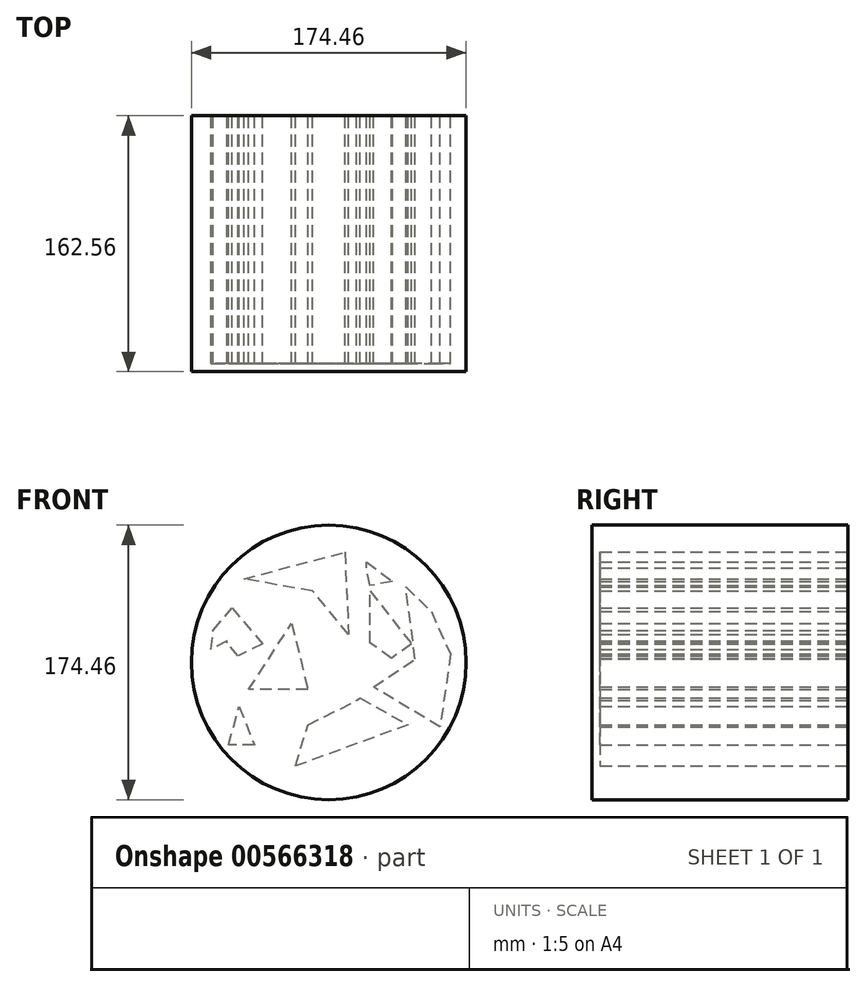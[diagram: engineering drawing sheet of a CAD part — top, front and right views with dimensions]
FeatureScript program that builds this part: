
annotation { "Feature Type Name" : "Feature", "Feature Type Description" : "" }
export const myFeature = defineFeature(function(context is Context, id is Id, definition is map)
    precondition{}
    {
        {
            var Q0;
            Q0=qCreatedBy(makeId("Front.planeOp"),FACE);
            var sketch = newSketch(context, id + "F0", { "sketchPlane" : qUnion([Q0])});
            skCircle(sketch, "E0", {"center": v(0, 2.96) * mm, "radius": 76.39 * mm});
            skLineSegment(sketch, "E1", {"start": v(-74.5, 19.82) * mm, "end": v(-55.23, 19.82) * mm});
            skLineSegment(sketch, "E2", {"start": v(-55.23, 19.82) * mm, "end": v(-44.99, 9.16) * mm});
            skLineSegment(sketch, "E3", {"start": v(-44.99, 9.16) * mm, "end": v(-44.99, -5.66) * mm});
            skLineSegment(sketch, "E4", {"start": v(-44.99, -5.66) * mm, "end": v(-22.1, -5.66) * mm});
            skLineSegment(sketch, "E5", {"start": v(-22.1, -3.5) * mm, "end": v(-22.1, 12.4) * mm});
            skLineSegment(sketch, "E6", {"start": v(-21.28, 11.85) * mm, "end": v(-3.77, 16.7) * mm});
            skLineSegment(sketch, "E7", {"start": v(-3.77, 16.7) * mm, "end": v(2.7, 35.83) * mm});
            skLineSegment(sketch, "E8", {"start": v(2.7, 35.83) * mm, "end": v(25.6, 35.83) * mm});
            skLineSegment(sketch, "E9", {"start": v(25.6, 35.83) * mm, "end": v(-12.12, 57.65) * mm});
            skLineSegment(sketch, "E10", {"start": v(-12.12, 57.65) * mm, "end": v(20.33, 76.6) * mm});
            skLineSegment(sketch, "E11", {"start": v(-3.77, 16.7) * mm, "end": v(32.87, 9.16) * mm});
            skLineSegment(sketch, "E12", {"start": v(32.87, 9.16) * mm, "end": v(28.86, -10.3) * mm});
            skLineSegment(sketch, "E13", {"start": v(29.9, -10.5) * mm, "end": v(54.69, -10.5) * mm});
            skLineSegment(sketch, "E14", {"start": v(54.69, -10.5) * mm, "end": v(11.58, -43.37) * mm});
            skLineSegment(sketch, "E15", {"start": v(11.58, -43.37) * mm, "end": v(42.3, -49.84) * mm});
            skLineSegment(sketch, "E16", {"start": v(42.3, -49.84) * mm, "end": v(54.69, -35.56) * mm});
            skLineSegment(sketch, "E17", {"start": v(55.76, -35.56) * mm, "end": v(63.58, -38.8) * mm});
            skLineSegment(sketch, "E18", {"start": v(-22.1, -3.5) * mm, "end": v(-22.1, -5.66) * mm});
            skLineSegment(sketch, "E19", {"start": v(-44.99, -5.66) * mm, "end": v(-27.75, -45.8) * mm});
            skLineSegment(sketch, "E20", {"start": v(-27.75, -45.8) * mm, "end": v(-3.77, -24.51) * mm});
            skLineSegment(sketch, "E21", {"start": v(-3.77, -24.51) * mm, "end": v(25.6, -32.7) * mm});
            skLineSegment(sketch, "E22", {"start": v(-21.28, 11.85) * mm, "end": v(-36.9, 38.25) * mm});
            skLineSegment(sketch, "E23", {"start": v(-36.9, 38.25) * mm, "end": v(2.7, 35.83) * mm});
            skLineSegment(sketch, "E24", {"start": v(-36.9, 38.25) * mm, "end": v(-51.77, 42.4) * mm});
            skLineSegment(sketch, "E25", {"start": v(-51.45, 42.56) * mm, "end": v(-31.05, 72.75) * mm});
            skLineSegment(sketch, "E26", {"start": v(25.6, 35.83) * mm, "end": v(48.22, 16.7) * mm});
            skLineSegment(sketch, "E27", {"start": v(48.22, 16.7) * mm, "end": v(62.82, 46.42) * mm});
            skLineSegment(sketch, "E28", {"start": v(-36.89, -24.51) * mm, "end": v(-61.06, -42.94) * mm});
            skLineSegment(sketch, "E29", {"start": v(-22.1, -40.78) * mm, "end": v(20.33, -52.59) * mm});
            skLineSegment(sketch, "E30", {"start": v(20.33, -54.96) * mm, "end": v(-8.08, -73) * mm});
            skLineSegment(sketch, "E31", {"start": v(20.33, -52.59) * mm, "end": v(20.33, -54.96) * mm});
            skLineSegment(sketch, "E32", {"start": v(32.87, 9.16) * mm, "end": v(54.69, 9.16) * mm});
            skLineSegment(sketch, "E33", {"start": v(53.88, 8.62) * mm, "end": v(48.22, 16.7) * mm});
            skSolve(sketch);
        }
        {
            var Q0;
            Q0=qCreatedBy(makeId("Front.planeOp"),FACE);
            var sketch = newSketch(context, id + "F1", { "sketchPlane" : qUnion([Q0])});
            skCircle(sketch, "E34", {"center": v(0, 0) * mm, "radius": 87.23 * mm});
            skLineSegment(sketch, "E35", {"start": v(60.07, 50.38) * mm, "end": v(46.6, 24.79) * mm});
            skLineSegment(sketch, "E36", {"start": v(46.6, 24.79) * mm, "end": v(0, 56.04) * mm});
            skLineSegment(sketch, "E37", {"start": v(0, 56.04) * mm, "end": v(24.25, 75.97) * mm});
            skLineSegment(sketch, "E38", {"start": v(65.46, -35.83) * mm, "end": v(51.45, -30.71) * mm});
            skLineSegment(sketch, "E39", {"start": v(51.45, -30.71) * mm, "end": v(42.03, -42.03) * mm});
            skLineSegment(sketch, "E40", {"start": v(42.03, -42.03) * mm, "end": v(24.25, -42.03) * mm});
            skLineSegment(sketch, "E41", {"start": v(25.86, -41.22) * mm, "end": v(61.15, -7.81) * mm});
            skLineSegment(sketch, "E42", {"start": v(61.15, -7.81) * mm, "end": v(35.83, -7.81) * mm});
            skLineSegment(sketch, "E43", {"start": v(35.83, -7.27) * mm, "end": v(35.83, 5.12) * mm});
            skLineSegment(sketch, "E44", {"start": v(36.1, 5.12) * mm, "end": v(60.07, 5.12) * mm});
            skLineSegment(sketch, "E45", {"start": v(60.07, 6.2) * mm, "end": v(56.03, 15.09) * mm});
            skLineSegment(sketch, "E46", {"start": v(56.03, 15.09) * mm, "end": v(65.73, 41.76) * mm});
            skLineSegment(sketch, "E47", {"start": v(-14.82, -71.93) * mm, "end": v(11.58, -54.42) * mm});
            skLineSegment(sketch, "E48", {"start": v(11.58, -54.42) * mm, "end": v(-22.36, -45.53) * mm});
            skLineSegment(sketch, "E49", {"start": v(-22.36, -45.53) * mm, "end": v(-29.36, -50.38) * mm});
            skLineSegment(sketch, "E50", {"start": v(-29.36, -50.38) * mm, "end": v(-37.45, -32.06) * mm});
            skLineSegment(sketch, "E51", {"start": v(-37.45, -32.06) * mm, "end": v(-56.84, -46.88) * mm});
            skLineSegment(sketch, "E52", {"start": v(-64.92, -36.64) * mm, "end": v(-44.72, -22.63) * mm});
            skLineSegment(sketch, "E53", {"start": v(-44.72, -22.63) * mm, "end": v(-51.18, 8.62) * mm});
            skLineSegment(sketch, "E54", {"start": v(-51.18, 8.62) * mm, "end": v(-56.84, 14.55) * mm});
            skLineSegment(sketch, "E55", {"start": v(-58.46, 14.55) * mm, "end": v(-74.9, 14.55) * mm});
            skLineSegment(sketch, "E56", {"start": v(-41.76, 66.81) * mm, "end": v(-56.84, 40.95) * mm});
            skLineSegment(sketch, "E57", {"start": v(-55.76, 40.95) * mm, "end": v(-40.4, 36.1) * mm});
            skLineSegment(sketch, "E58", {"start": v(-40.4, 36.1) * mm, "end": v(-25.05, 12.12) * mm});
            skLineSegment(sketch, "E59", {"start": v(-25.05, 12.12) * mm, "end": v(-25.05, 0) * mm});
            skLineSegment(sketch, "E60", {"start": v(-24.78, -1.35) * mm, "end": v(-40.4, -1.35) * mm});
            skLineSegment(sketch, "E61", {"start": v(-39.6, -1.35) * mm, "end": v(-44.72, -5.12) * mm});
            skLineSegment(sketch, "E62", {"start": v(0, 33.68) * mm, "end": v(-6.47, 21.28) * mm});
            skLineSegment(sketch, "E63", {"start": v(-6.47, 21.28) * mm, "end": v(-20.07, 12.57) * mm});
            skLineSegment(sketch, "E64", {"start": v(0, 33.68) * mm, "end": v(-33.67, 33.68) * mm});
            skLineSegment(sketch, "E65", {"start": v(22.1, -35.3) * mm, "end": v(-2.42, -28.02) * mm});
            skLineSegment(sketch, "E66", {"start": v(-2.42, -28.02) * mm, "end": v(-17.24, -41.22) * mm});
            skSolve(sketch);
        }
        {
            var Q0;
            Q0=makeQuery(id+"F0.imprint","IMPRINT",FACE,{"disambiguationData":[TD([[makeQuery(id+"F0.imprint","IMPRINT",EDGE,{"derivedFrom":sQuery(id+"F0.wireOp",EDGE,"E6")}),1.0]])]});
            var Q1;
            Q1=makeQuery(id+"F1.imprint","IMPRINT",FACE,{"disambiguationData":[TD([[makeQuery(id+"F1.imprint","IMPRINT",EDGE,{"derivedFrom":sQuery(id+"F1.wireOp",EDGE,"E34")}),1.0]])]});
            extrude(context, id + "F2", {"entities" : qUnion([Q0, Q1]), "depth" : 162.56 * mm, "offsetDistance" : 25.4 * mm});
        }
        {
            var Q0;
            Q0=makeQuery(id+"F2.opExtrude","SWEPT_BODY",BODY,{"disambiguationData":[OSD([sQuery(id+"F0.wireOp",EDGE,"E6"),sQuery(id+"F0.wireOp",EDGE,"E7"),sQuery(id+"F0.wireOp",EDGE,"E22"),sQuery(id+"F0.wireOp",EDGE,"E23")])]});
            deleteBodies(context, id + "F3", {"entities" : qUnion([Q0])});
        }
        {
            var Q0;
            Q0=makeQuery(id+"F2.opExtrude","CAP_FACE",FACE,{"disambiguationData":[OSD([sQuery(id+"F1.wireOp",EDGE,"E34")])],"isStart":true});
            var sketch = newSketch(context, id + "F4", { "sketchPlane" : qUnion([Q0])});
            skLineSegment(sketch, "E67", {"start": v(-52.46, 11.85) * mm, "end": v(-39.8, 2.7) * mm});
            skLineSegment(sketch, "E68", {"start": v(-39.8, 2.7) * mm, "end": v(-26.33, 12.4) * mm});
            skLineSegment(sketch, "E69", {"start": v(-26.33, 12.4) * mm, "end": v(-26.33, 46.07) * mm});
            skLineSegment(sketch, "E70", {"start": v(-25.79, 46.07) * mm, "end": v(-52.46, 11.85) * mm});
            skSolve(sketch);
        }
        {
            var Q0;
            {var subQ0=sQuery(id+"F4.wireOp",EDGE,"E67");Q0=makeQuery(id+"F4.imprint","IMPRINT",FACE,{"disambiguationData":[TD([[makeQuery(id+"F4.imprint","IMPRINT",EDGE,{"derivedFrom":subQ0}),1.0]])]});}
            extrude(context, id + "F5", {"entities" : qUnion([Q0]), "operationType" : NewBodyOperationType.REMOVE, "oppositeDirection" : true, "depth" : 157.48 * mm, "offsetDistance" : 25.4 * mm});
        }
        {
            var Q0;
            Q0=makeQuery(id+"F2.opExtrude","CAP_FACE",FACE,{"disambiguationData":[OSD([sQuery(id+"F1.wireOp",EDGE,"E34")])],"isStart":true});
            var sketch = newSketch(context, id + "F6", { "sketchPlane" : qUnion([Q0])});
            skLineSegment(sketch, "E71", {"start": v(-19.86, -22.63) * mm, "end": v(-50.3, -39.6) * mm});
            skLineSegment(sketch, "E72", {"start": v(-50.3, -39.6) * mm, "end": v(21.09, -65.74) * mm});
            skLineSegment(sketch, "E73", {"start": v(21.09, -65.74) * mm, "end": v(13.27, -39.6) * mm});
            skLineSegment(sketch, "E74", {"start": v(13.27, -39.6) * mm, "end": v(-17.7, -24.25) * mm});
            skLineSegment(sketch, "E75", {"start": v(-17.7, -24.25) * mm, "end": v(-19.86, -22.63) * mm});
            skLineSegment(sketch, "E76", {"start": v(23.51, 24.79) * mm, "end": v(13.27, -17.24) * mm});
            skLineSegment(sketch, "E77", {"start": v(13.27, -17.24) * mm, "end": v(50.99, -17.24) * mm});
            skLineSegment(sketch, "E78", {"start": v(50.99, -17.24) * mm, "end": v(23.51, 24.79) * mm});
            skLineSegment(sketch, "E79", {"start": v(10.31, 45.38) * mm, "end": v(53.95, 53.07) * mm});
            skLineSegment(sketch, "E80", {"start": v(53.95, 53.07) * mm, "end": v(-10.16, 70.05) * mm});
            skLineSegment(sketch, "E81", {"start": v(-10.16, 70.05) * mm, "end": v(-12.59, 17.78) * mm});
            skLineSegment(sketch, "E82", {"start": v(-12.59, 17.78) * mm, "end": v(10.31, 45.38) * mm});
            skLineSegment(sketch, "E83", {"start": v(-74, 21.28) * mm, "end": v(-81.28, -4.31) * mm});
            skLineSegment(sketch, "E84", {"start": v(-81.28, -4.31) * mm, "end": v(-69.7, -35.02) * mm});
            skLineSegment(sketch, "E85", {"start": v(-69.7, -35.02) * mm, "end": v(-33.86, -15.04) * mm});
            skLineSegment(sketch, "E86", {"start": v(-34.14, -14.28) * mm, "end": v(-63.23, 11.85) * mm});
            skLineSegment(sketch, "E87", {"start": v(-63.23, 11.85) * mm, "end": v(-50.3, 33.4) * mm});
            skLineSegment(sketch, "E88", {"start": v(-49.5, 33.4) * mm, "end": v(-74, 21.28) * mm});
            skLineSegment(sketch, "E89", {"start": v(61.5, 34.75) * mm, "end": v(42.1, 11.85) * mm});
            skLineSegment(sketch, "E90", {"start": v(42.1, 11.85) * mm, "end": v(57.53, 4.2) * mm});
            skLineSegment(sketch, "E91", {"start": v(57.53, 4.2) * mm, "end": v(64.73, 12.4) * mm});
            skLineSegment(sketch, "E92", {"start": v(64.73, 13.74) * mm, "end": v(74.7, 8.35) * mm});
            skLineSegment(sketch, "E93", {"start": v(74.7, 8.35) * mm, "end": v(73.35, 20.48) * mm});
            skLineSegment(sketch, "E94", {"start": v(73.35, 20.48) * mm, "end": v(61.5, 34.75) * mm});
            skLineSegment(sketch, "E95", {"start": v(64.73, 12.4) * mm, "end": v(64.73, 13.74) * mm});
            skSolve(sketch);
        }
        {
            var Q0;
            Q0=makeQuery(id+"F6.imprint","IMPRINT",FACE,{"disambiguationData":[TD([[makeQuery(id+"F6.imprint","IMPRINT",EDGE,{"derivedFrom":sQuery(id+"F6.wireOp",EDGE,"E79")}),1.0]])]});
            var Q1;
            Q1=makeQuery(id+"F6.imprint","IMPRINT",FACE,{"disambiguationData":[TD([[makeQuery(id+"F6.imprint","IMPRINT",EDGE,{"derivedFrom":sQuery(id+"F6.wireOp",EDGE,"E76")}),1.0]])]});
            var Q2;
            Q2=makeQuery(id+"F6.imprint","IMPRINT",FACE,{"disambiguationData":[TD([[makeQuery(id+"F6.imprint","IMPRINT",EDGE,{"derivedFrom":sQuery(id+"F6.wireOp",EDGE,"E89")}),1.0]])]});
            var Q3;
            Q3=makeQuery(id+"F6.imprint","IMPRINT",FACE,{"disambiguationData":[TD([[makeQuery(id+"F6.imprint","IMPRINT",EDGE,{"derivedFrom":sQuery(id+"F6.wireOp",EDGE,"E71")}),1.0]])]});
            extrude(context, id + "F7", {"entities" : qUnion([Q0, Q1, Q2, Q3]), "operationType" : NewBodyOperationType.REMOVE, "oppositeDirection" : true, "depth" : 157.48 * mm, "offsetDistance" : 25.4 * mm});
        }
        {
            var Q0;
            Q0=makeQuery(id+"F2.opExtrude","CAP_FACE",FACE,{"disambiguationData":[OSD([sQuery(id+"F1.wireOp",EDGE,"E34")])],"isStart":true});
            var sketch = newSketch(context, id + "F8", { "sketchPlane" : qUnion([Q0])});
            skLineSegment(sketch, "E96", {"start": v(-65.12, 32.33) * mm, "end": v(-77.24, 5.39) * mm});
            skLineSegment(sketch, "E97", {"start": v(-77.24, 5.39) * mm, "end": v(-70.78, -40.95) * mm});
            skLineSegment(sketch, "E98", {"start": v(-70.78, -40.95) * mm, "end": v(-28.48, -15.63) * mm});
            skLineSegment(sketch, "E99", {"start": v(-28.48, -15.63) * mm, "end": v(-54.88, 2.15) * mm});
            skLineSegment(sketch, "E100", {"start": v(-54.88, 2.15) * mm, "end": v(-48.96, 48.23) * mm});
            skLineSegment(sketch, "E101", {"start": v(-48.96, 47.96) * mm, "end": v(-65.12, 32.33) * mm});
            skLineSegment(sketch, "E102", {"start": v(-23.9, 63.85) * mm, "end": v(-40.34, 51.46) * mm});
            skLineSegment(sketch, "E103", {"start": v(-40.34, 51.46) * mm, "end": v(-26.06, 48.76) * mm});
            skLineSegment(sketch, "E104", {"start": v(-26.06, 48.76) * mm, "end": v(-23.9, 60.19) * mm});
            skLineSegment(sketch, "E105", {"start": v(-23.9, 60.19) * mm, "end": v(-23.9, 63.85) * mm});
            skLineSegment(sketch, "E106", {"start": v(11.12, 29.9) * mm, "end": v(-23.9, -2.7) * mm});
            skLineSegment(sketch, "E107", {"start": v(-23.36, -3.5) * mm, "end": v(-6.66, -22.63) * mm});
            skLineSegment(sketch, "E108", {"start": v(-6.66, -22.63) * mm, "end": v(11.12, 29.9) * mm});
            skLineSegment(sketch, "E109", {"start": v(56.92, -28.02) * mm, "end": v(47.22, -52.27) * mm});
            skLineSegment(sketch, "E110", {"start": v(47.22, -52.27) * mm, "end": v(63.65, -52.27) * mm});
            skLineSegment(sketch, "E111", {"start": v(63.65, -52.27) * mm, "end": v(56.92, -28.02) * mm});
            skSolve(sketch);
        }
        {
            var Q0;
            {var subQ1=sQuery(id+"F8.wireOp",EDGE,"E96");Q0=makeQuery(id+"F8.imprint","IMPRINT",FACE,{"disambiguationData":[TD([[makeQuery(id+"F8.imprint","IMPRINT",EDGE,{"derivedFrom":subQ1}),1.0]])]});}
            var Q1;
            Q1=makeQuery(id+"F8.imprint","IMPRINT",FACE,{"disambiguationData":[TD([[makeQuery(id+"F8.imprint","IMPRINT",EDGE,{"derivedFrom":sQuery(id+"F8.wireOp",EDGE,"E102")}),1.0]])]});
            var Q2;
            Q2=makeQuery(id+"F8.imprint","IMPRINT",FACE,{"disambiguationData":[TD([[makeQuery(id+"F8.imprint","IMPRINT",EDGE,{"derivedFrom":sQuery(id+"F8.wireOp",EDGE,"E109")}),1.0]])]});
            extrude(context, id + "F9", {"entities" : qUnion([Q0, Q1, Q2]), "operationType" : NewBodyOperationType.REMOVE, "oppositeDirection" : true, "depth" : 157.48 * mm, "offsetDistance" : 25.4 * mm});
        }
    });
